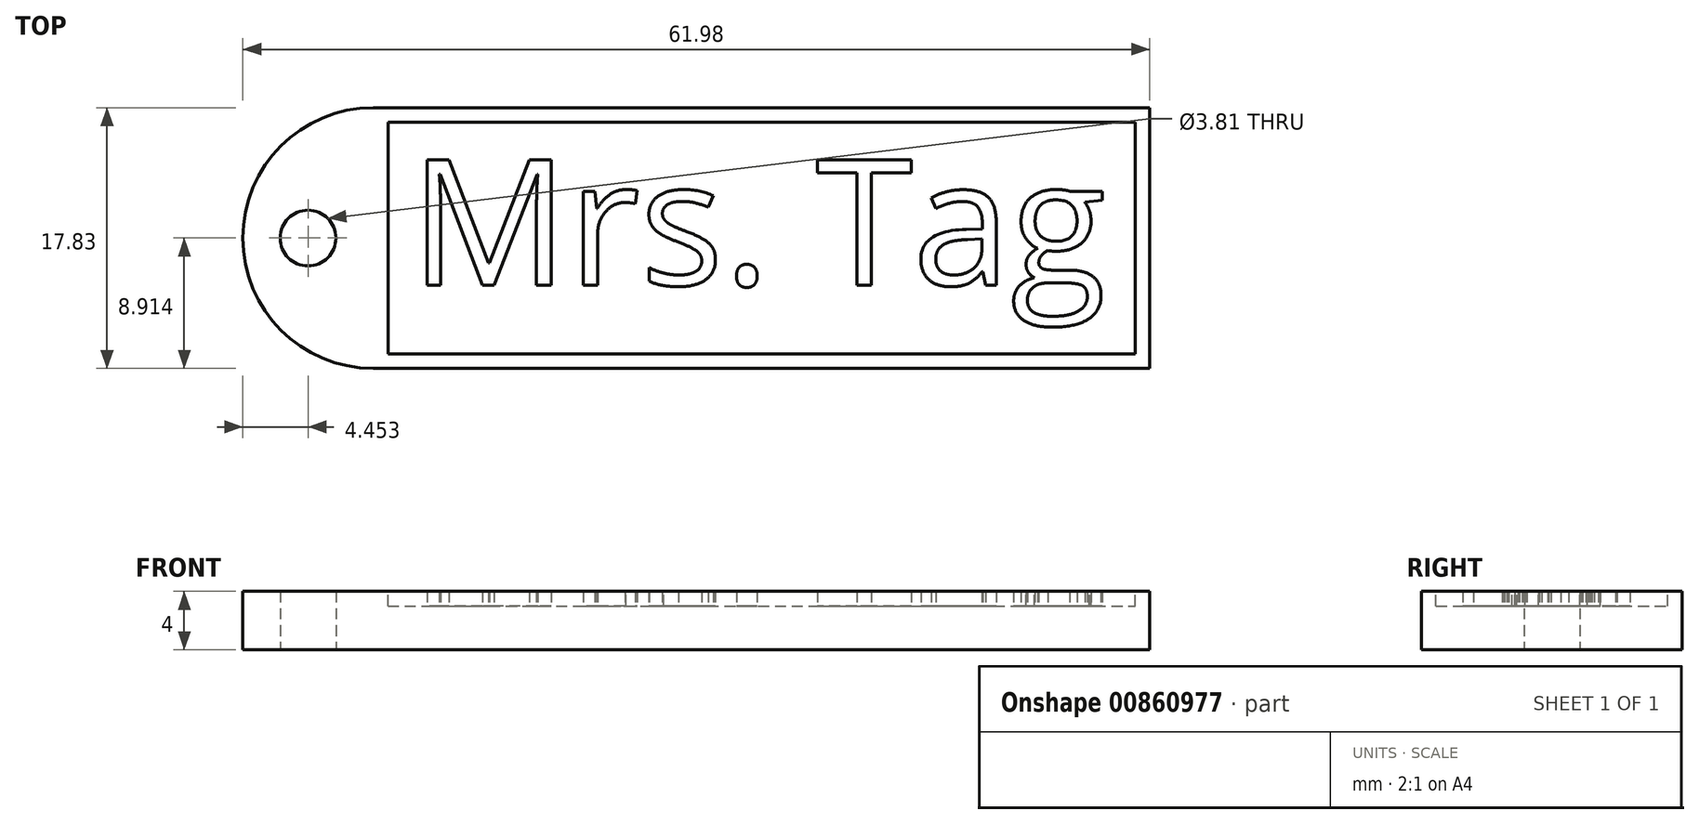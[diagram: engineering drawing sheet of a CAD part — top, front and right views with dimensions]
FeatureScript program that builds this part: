
annotation { "Feature Type Name" : "Feature", "Feature Type Description" : "" }
export const myFeature = defineFeature(function(context is Context, id is Id, definition is map)
    precondition{}
    {
        {
            var Q0;
            Q0=qCreatedBy(makeId("Top.planeOp"),FACE);
            var sketch = newSketch(context, id + "F0", { "sketchPlane" : qUnion([Q0])});
            skLineSegment(sketch, "E0.bottom", {"start": v(0, 0) * mm, "end": v(53.07, 0) * mm});
            skLineSegment(sketch, "E0.top", {"start": v(0, 17.83) * mm, "end": v(53.07, 17.83) * mm});
            skLineSegment(sketch, "E0.right", {"start": v(53.07, 0) * mm, "end": v(53.07, 17.83) * mm});
            skArc(sketch, "E1", {"start": v(0, 17.83) * mm, "mid": v(-8.91, 8.91) * mm, "end": v(0, 0) * mm});
            skLineSegment(sketch, "E2", {"start": v(0, 8.91) * mm, "end": v(-8.91, 8.91) * mm, "construction": true});
            skCircle(sketch, "E3", {"center": v(-4.46, 8.91) * mm, "radius": 1.9 * mm});
            skSolve(sketch);
        }
        {
            var Q0;
            Q0=makeQuery(id+"F0.imprint","IMPRINT",FACE,{"disambiguationData":[TD([[makeQuery(id+"F0.imprint","IMPRINT",EDGE,{"derivedFrom":sQuery(id+"F0.wireOp",EDGE,"E0.bottom")}),1.0]])]});
            extrude(context, id + "F1", {"entities" : qUnion([Q0]), "depth" : 4 * mm, "offsetDistance" : 25 * mm});
        }
        {
            var Q0;
            Q0=makeQuery(id+"F1.opExtrude","CAP_FACE",FACE,{"disambiguationData":[OSD([sQuery(id+"F0.wireOp",EDGE,"E0.bottom"),sQuery(id+"F0.wireOp",EDGE,"E0.top"),sQuery(id+"F0.wireOp",EDGE,"E0.right"),sQuery(id+"F0.wireOp",EDGE,"E1"),sQuery(id+"F0.wireOp",EDGE,"E3")])],"isStart":false});
            var sketch = newSketch(context, id + "F2", { "sketchPlane" : qUnion([Q0])});
            skLineSegment(sketch, "E4.bottom", {"start": v(1, 1) * mm, "end": v(52.07, 1) * mm});
            skLineSegment(sketch, "E4.top", {"start": v(1, 16.83) * mm, "end": v(52.07, 16.83) * mm});
            skLineSegment(sketch, "E4.left", {"start": v(1, 1) * mm, "end": v(1, 16.83) * mm});
            skLineSegment(sketch, "E4.right", {"start": v(52.07, 1) * mm, "end": v(52.07, 16.83) * mm});
            skSolve(sketch);
        }
        {
            var Q0;
            Q0 = qSketchRegion(id + "F2", true);
            extrude(context, id + "F3", {"entities" : qUnion([Q0]), "operationType" : NewBodyOperationType.REMOVE, "oppositeDirection" : true, "depth" : 1 * mm, "offsetDistance" : 25 * mm});
        }
        {
            var Q0;
            Q0=makeQuery(id+"F3.boolean.opBoolean","COPY",FACE,{"derivedFrom":makeQuery(id+"F3.opExtrude","CAP_FACE",FACE,{"disambiguationData":[OSD([sQuery(id+"F2.wireOp",EDGE,"E4.bottom"),sQuery(id+"F2.wireOp",EDGE,"E4.top"),sQuery(id+"F2.wireOp",EDGE,"E4.left"),sQuery(id+"F2.wireOp",EDGE,"E4.right")])],"isStart":false})});
            var sketch = newSketch(context, id + "F4", { "sketchPlane" : qUnion([Q0])});
            skText(sketch, "E5", { "text": "Mrs. Tag", "fontName": "OpenSans-Regular.ttf"});
            const initialGuessF4  = {"E5": [0.0025, 0.0057, 1, 0, 0.00863]};
            skSetInitialGuess(sketch, initialGuessF4);
            skSolve(sketch);
        }
        {
            var Q0;
            Q0 = qSketchRegion(id + "F4", true);
            extrude(context, id + "F5", {"entities" : qUnion([Q0]), "operationType" : NewBodyOperationType.ADD, "depth" : 1 * mm, "offsetDistance" : 25 * mm});
        }
    });
